# Revit family: Shower_Outlet_Elbow-GROHE-Tempesta-26636_Series
name_source: partatom
category: Plumbing Fixtures
units: mm (PartAtom-declared; Revit-internal decimal feet)

## family parameters
Cut with Voids When Loaded = No
Host = Face
OmniClass Number = 23.45.05.14.17
OmniClass Title = Showers
Part Type = Normal
Room Calculation Point = No
Round Connector Dimension = Use Diameter
Shared = Yes

## types (3) — shared parameters
Adjustable Outlet Constraint = 1 3/8"
Adjustable Outlet Width = 1 3/8"
Assembly Code = D2010710
CW Connection = No
CWFU = 3
Compliance Certifications = Massachusetts Plumbing Board Approved
Default Elevation = 0"
Description = Tempesta Wall Union
Diameter = 2 5/8"
HW Connection = No
HWFU = 3
Installation Type = Wall Mounted
Manufacturer = Grohe
Tempered Connection Diameter = 1/2"
Tempered Water Connection = Yes
URL = https://www.grohe.com
Vent Connection = No
WFU = 4
Waste Connection = No
Width = 2 9/16"

## per-type parameters (varying)
| type | Finish | Material |
| 26636001 | Metal-Grohe-001-Chrome | Metal-Grohe-001-Chrome |
| 266362431 | Metal-Grohe-2431-Matte Black | Metal-Grohe-2431-Matte Black |
| 26636EN1 | Plasstic-Grohe-EN1-Brushed Nickel Infinity Finish | Plasstic-Grohe-EN1-Brushed Nickel Infinity Finish |

note: column(s) folded — value = type name in every type: Model

## geometry (parser evidence)
native form markers: Sweep x3
no freeform markers — native parametric forms only
